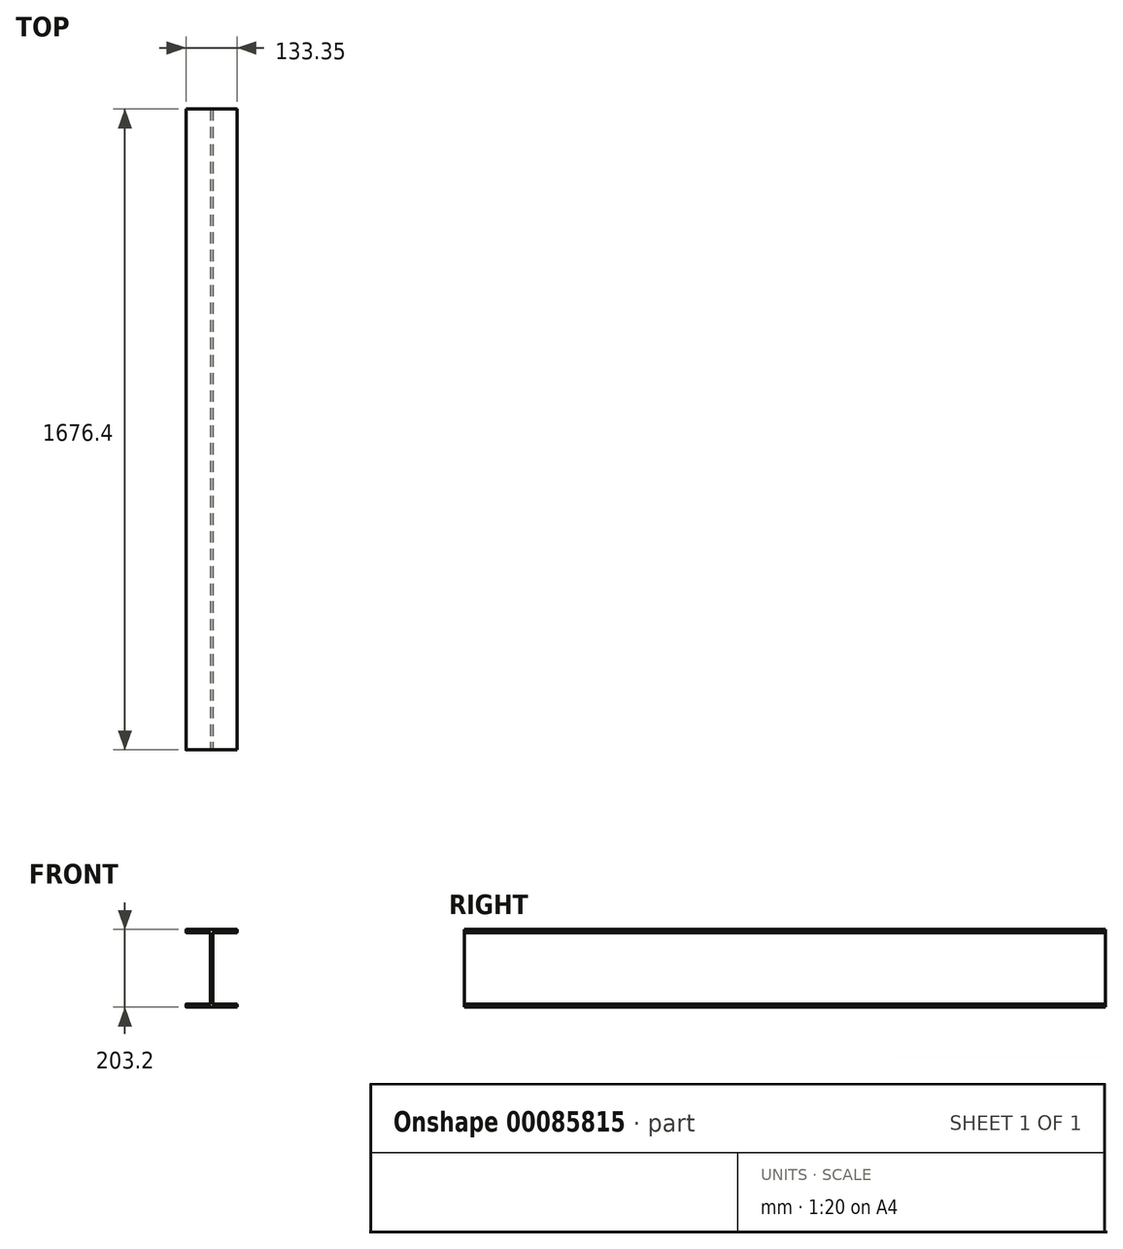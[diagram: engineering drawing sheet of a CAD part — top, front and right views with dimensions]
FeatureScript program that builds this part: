
annotation { "Feature Type Name" : "Feature", "Feature Type Description" : "" }
export const myFeature = defineFeature(function(context is Context, id is Id, definition is map)
    precondition{}
    {
        {
            var Q0;
            Q0=qCreatedBy(makeId("Front.planeOp"),FACE);
            var sketch = newSketch(context, id + "F0", { "sketchPlane" : qUnion([Q0])});
            skPoint(sketch, "E0.middle", {"position": v(0, 0) * mm});
            skLineSegment(sketch, "E1.bottom", {"start": v(-65.91, 93.22) * mm, "end": v(-3.68, 93.22) * mm});
            skLineSegment(sketch, "E1.top", {"start": v(-65.91, 101.6) * mm, "end": v(65.91, 101.6) * mm});
            skLineSegment(sketch, "E1.left", {"start": v(-66.68, 93.98) * mm, "end": v(-66.68, 100.84) * mm});
            skLineSegment(sketch, "E1.right", {"start": v(66.67, 93.98) * mm, "end": v(66.67, 100.84) * mm});
            skPoint(sketch, "E1.middle", {"position": v(0, 97.4) * mm});
            skLineSegment(sketch, "E2.MirrorCS", {"start": v(-65.91, -93.22) * mm, "end": v(-3.68, -93.22) * mm});
            skLineSegment(sketch, "E3.MirrorCS", {"start": v(-66.68, -93.98) * mm, "end": v(-66.68, -100.84) * mm});
            skLineSegment(sketch, "E4.MirrorCS", {"start": v(-65.91, -101.6) * mm, "end": v(65.91, -101.6) * mm});
            skLineSegment(sketch, "E5.MirrorCS", {"start": v(66.67, -93.98) * mm, "end": v(66.67, -100.84) * mm});
            skPoint(sketch, "E6.visualSharp", {"position": v(-66.68, 101.6) * mm});
            skArc(sketch, "E6.filletArc", {"start": v(-65.91, 101.6) * mm, "mid": v(-66.45, 101.38) * mm, "end": v(-66.68, 100.84) * mm});
            skPoint(sketch, "E7.visualSharp", {"position": v(-66.68, 93.22) * mm});
            skArc(sketch, "E7.filletArc", {"start": v(-66.68, 93.98) * mm, "mid": v(-66.45, 93.44) * mm, "end": v(-65.91, 93.22) * mm});
            skPoint(sketch, "E8.visualSharp", {"position": v(66.67, 93.22) * mm});
            skArc(sketch, "E8.filletArc", {"start": v(65.91, 93.22) * mm, "mid": v(66.45, 93.44) * mm, "end": v(66.67, 93.98) * mm});
            skPoint(sketch, "E9.visualSharp", {"position": v(66.67, 101.6) * mm});
            skArc(sketch, "E9.filletArc", {"start": v(66.67, 100.84) * mm, "mid": v(66.45, 101.38) * mm, "end": v(65.91, 101.6) * mm});
            skPoint(sketch, "E10", {"position": v(2.92, 93.22) * mm});
            skPoint(sketch, "E11", {"position": v(-2.92, 93.22) * mm});
            skPoint(sketch, "E12", {"position": v(-2.92, -93.22) * mm});
            skPoint(sketch, "E13", {"position": v(2.92, -93.22) * mm});
            skLineSegment(sketch, "E14", {"start": v(2.92, -92.46) * mm, "end": v(2.92, 92.46) * mm});
            skLineSegment(sketch, "E15", {"start": v(-2.92, 92.46) * mm, "end": v(-2.92, -92.46) * mm});
            skArc(sketch, "E16.filletArc", {"start": v(-2.92, 92.46) * mm, "mid": v(-3.14, 93) * mm, "end": v(-3.68, 93.22) * mm});
            skLineSegment(sketch, "E17", {"start": v(3.68, 93.22) * mm, "end": v(65.91, 93.22) * mm});
            skArc(sketch, "E18.filletArc", {"start": v(3.68, 93.22) * mm, "mid": v(3.14, 93) * mm, "end": v(2.92, 92.46) * mm});
            skLineSegment(sketch, "E19", {"start": v(3.68, -93.22) * mm, "end": v(65.91, -93.22) * mm});
            skArc(sketch, "E20.filletArc", {"start": v(-3.68, -93.22) * mm, "mid": v(-3.14, -93) * mm, "end": v(-2.92, -92.46) * mm});
            skPoint(sketch, "E21.newPointB", {"position": v(0, -93.22) * mm});
            skArc(sketch, "E21.filletArc", {"start": v(2.92, -92.46) * mm, "mid": v(3.14, -93) * mm, "end": v(3.68, -93.22) * mm});
            skPoint(sketch, "E22.visualSharp", {"position": v(-66.68, -93.22) * mm});
            skArc(sketch, "E22.filletArc", {"start": v(-65.91, -93.22) * mm, "mid": v(-66.45, -93.44) * mm, "end": v(-66.68, -93.98) * mm});
            skPoint(sketch, "E23.visualSharp", {"position": v(66.67, -101.6) * mm});
            skArc(sketch, "E23.filletArc", {"start": v(65.91, -101.6) * mm, "mid": v(66.45, -101.38) * mm, "end": v(66.67, -100.84) * mm});
            skPoint(sketch, "E24.visualSharp", {"position": v(66.67, -93.22) * mm});
            skArc(sketch, "E24.filletArc", {"start": v(66.67, -93.98) * mm, "mid": v(66.45, -93.44) * mm, "end": v(65.91, -93.22) * mm});
            skPoint(sketch, "E25.visualSharp", {"position": v(-66.68, -101.6) * mm});
            skArc(sketch, "E25.filletArc", {"start": v(-66.68, -100.84) * mm, "mid": v(-66.45, -101.38) * mm, "end": v(-65.91, -101.6) * mm});
            skSolve(sketch);
        }
        {
            var Q0;
            Q0=makeQuery(id+"F0.imprint","IMPRINT",FACE,{"disambiguationData":[TD([[makeQuery(id+"F0.imprint","IMPRINT",EDGE,{"derivedFrom":sQuery(id+"F0.wireOp",EDGE,"E1.bottom")}),1.0]])]});
            extrude(context, id + "F1", {"entities" : qUnion([Q0]), "oppositeDirection" : true, "depth" : 1676.4 * mm, "offsetDistance" : 25.4 * mm});
        }
        {
            var Q0;
            Q0=makeQuery(id+"F1.opExtrude","SWEPT_FACE",FACE,{"disambiguationData":[OSD([sQuery(id+"F0.wireOp",EDGE,"E14")])]});
            var sketch = newSketch(context, id + "F2", { "sketchPlane" : qUnion([Q0])});
            skLineSegment(sketch, "E26", {"start": v(838.2, 92.46) * mm, "end": v(838.2, -92.46) * mm});
            skSolve(sketch);
        }
    });
